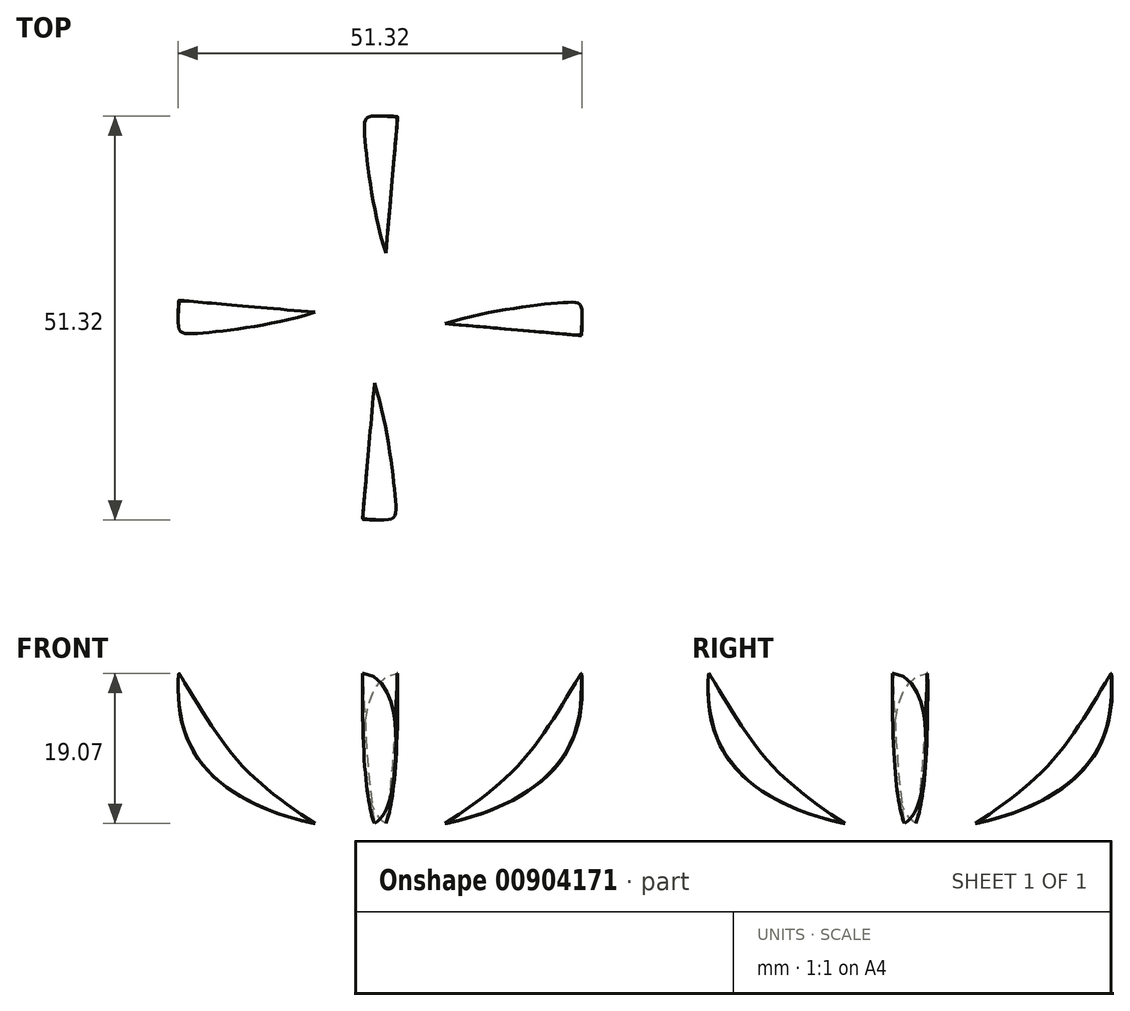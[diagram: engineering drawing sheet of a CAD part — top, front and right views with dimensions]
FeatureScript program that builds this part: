
annotation { "Feature Type Name" : "Feature", "Feature Type Description" : "" }
export const myFeature = defineFeature(function(context is Context, id is Id, definition is map)
    precondition{}
    {
        {
            var Q0;
            Q0=qCreatedBy(makeId("Front.planeOp"),FACE);
            var sketch = newSketch(context, id + "F0", { "sketchPlane" : qUnion([Q0])});
            skLineSegment(sketch, "E0", {"start": v(-28.58, 0) * mm, "end": v(28.58, 0) * mm, "construction": true});
            skLineSegment(sketch, "E1", {"start": v(0, 0) * mm, "end": v(0, -50.8) * mm, "construction": true});
            skLineSegment(sketch, "E2", {"start": v(-12.7, -50.8) * mm, "end": v(12.7, -50.8) * mm, "construction": true});
            skLineSegment(sketch, "E3", {"start": v(0, 0) * mm, "end": v(0, -12.7) * mm, "construction": true});
            skLineSegment(sketch, "E4", {"start": v(-23.5, -12.7) * mm, "end": v(23.5, -12.7) * mm, "construction": true});
            skLineSegment(sketch, "E5", {"start": v(0, -50.8) * mm, "end": v(0, -38.1) * mm, "construction": true});
            skLineSegment(sketch, "E6", {"start": v(-25.4, -38.1) * mm, "end": v(25.4, -38.1) * mm, "construction": true});
            skLineSegment(sketch, "E7", {"start": v(0, -52.8) * mm, "end": v(0, -57.57) * mm, "construction": true});
            skLineSegment(sketch, "E8", {"start": v(-19.77, -52.8) * mm, "end": v(-17.38, -48.69) * mm, "construction": true});
            skLineSegment(sketch, "E9", {"start": v(-28.25, -13.02) * mm, "end": v(-23.5, -12.7) * mm, "construction": true});
            skLineSegment(sketch, "E10", {"start": v(23.5, -12.7) * mm, "end": v(28.25, -12.93) * mm, "construction": true});
            skLineSegment(sketch, "E11", {"start": v(-25.4, -38.1) * mm, "end": v(-29.76, -40.01) * mm, "construction": true});
            skLineSegment(sketch, "E12", {"start": v(25.4, -38.1) * mm, "end": v(30.07, -39.03) * mm, "construction": true});
            skLineSegment(sketch, "E13", {"start": v(16.77, -49.02) * mm, "end": v(19.05, -53.2) * mm, "construction": true});
            skLineSegment(sketch, "E14", {"start": v(-28.58, 0) * mm, "end": v(-34.9, -3.29) * mm, "construction": true});
            skLineSegment(sketch, "E15", {"start": v(28.58, 0) * mm, "end": v(34.58, -3.85) * mm, "construction": true});
            skLineSegment(sketch, "E16", {"start": v(0, -52.8) * mm, "end": v(0, -57.57) * mm});
            skFitSpline(sketch, "E17", {"points": [v(0, -57.57) * mm, v(19.05, -53.2) * mm, v(30.07, -39.03) * mm, v(28.25, -12.93) * mm, v(34.58, -3.85) * mm, v(28.57, 0) * mm, v(23.5, -12.7) * mm, v(25.4, -38.1) * mm, v(16.77, -49.02) * mm, v(0, -52.8) * mm, v(-17.38, -48.69) * mm, v(-25.4, -38.1) * mm, v(-23.5, -12.7) * mm, v(-28.57, 0) * mm, v(-34.9, -3.29) * mm, v(-28.25, -13.02) * mm, v(-29.76, -40.01) * mm, v(-19.77, -52.8) * mm, v(0, -57.57) * mm]});
            skLineSegment(sketch, "E18", {"start": v(-25.62, -32.87) * mm, "end": v(-29.42, -32.87) * mm, "construction": true});
            skFitSpline(sketch, "E19", {"points": [v(-25.62, -32.87) * mm, v(-4.79, -52.5) * mm], "startDerivative": vector(17.85, -29.52) * mm, "endDerivative": vector(38.14, -17.66) * mm});
            skSolve(sketch);
        }
        {
            var Q0;
            {var subQ0=sQuery(id+"F0.wireOp",EDGE,"j9txepCX-qMbL-OIfj-HFUU-9PL2DQeBk5dc");var subQ1=sQuery(id+"F0.wireOp",EDGE,"E17");var subQ3=makeQuery(id+"F0.imprint","INTERSECT",VERTEX,{"derivedFrom":[subQ1,subQ0]});Q0=makeQuery(id+"F0.imprint","IMPRINT",FACE,{"disambiguationData":[TD([[makeQuery(id+"F0.imprint","IMPRINT",EDGE,{"disambiguationData":[TD([[subQ3,-1.0]])],"derivedFrom":subQ1}),-1.0]])]});}
            var Q1;
            Q1=sQuery(id+"F0.wireOp",EDGE,"E1");
            revolve(context, id + "F1", {"surfaceOperationType" : NewSurfaceOperationType.NEW, "entities" : qUnion([Q0]), "axis" : qUnion([Q1]), "revolveType" : RevolveType.TWO_DIRECTIONS, "angle" : 5 * degree, "angleBack" : 355 * degree});
        }
        {
            var Q0;
            {var subQ0=sQuery(id+"F0.wireOp",EDGE,"j9txepCX-qMbL-OIfj-HFUU-9PL2DQeBk5dc");var subQ1=sQuery(id+"F0.wireOp",EDGE,"E17");var subQ3=makeQuery(id+"F0.imprint","INTERSECT",VERTEX,{"derivedFrom":[subQ1,subQ0]});Q0=makeQuery(id+"F0.imprint","IMPRINT",FACE,{"disambiguationData":[TD([[makeQuery(id+"F0.imprint","IMPRINT",EDGE,{"disambiguationData":[TD([[subQ3,-1.0]])],"derivedFrom":subQ1}),-1.0]])]});}
            var Q1;
            Q1=sQuery(id+"F0.wireOp",EDGE,"E5");
            revolve(context, id + "F2", {"surfaceOperationType" : NewSurfaceOperationType.NEW, "entities" : qUnion([Q0]), "axis" : qUnion([Q1]), "revolveType" : RevolveType.TWO_DIRECTIONS, "angle" : 185 * degree, "angleBack" : 175 * degree});
        }
        {
            var Q0;
            {var subQ0=sQuery(id+"F0.wireOp",EDGE,"j9txepCX-qMbL-OIfj-HFUU-9PL2DQeBk5dc");var subQ1=sQuery(id+"F0.wireOp",EDGE,"E17");var subQ3=makeQuery(id+"F0.imprint","INTERSECT",VERTEX,{"derivedFrom":[subQ1,subQ0]});Q0=makeQuery(id+"F0.imprint","IMPRINT",FACE,{"disambiguationData":[TD([[makeQuery(id+"F0.imprint","IMPRINT",EDGE,{"disambiguationData":[TD([[subQ3,-1.0]])],"derivedFrom":subQ1}),-1.0]])]});}
            var Q1;
            Q1=sQuery(id+"F0.wireOp",EDGE,"E5");
            revolve(context, id + "F3", {"surfaceOperationType" : NewSurfaceOperationType.NEW, "entities" : qUnion([Q0]), "axis" : qUnion([Q1]), "revolveType" : RevolveType.TWO_DIRECTIONS, "angle" : 275 * degree, "angleBack" : 265 * degree});
        }
        {
            var Q0;
            {var subQ0=sQuery(id+"F0.wireOp",EDGE,"j9txepCX-qMbL-OIfj-HFUU-9PL2DQeBk5dc");var subQ1=sQuery(id+"F0.wireOp",EDGE,"E17");var subQ3=makeQuery(id+"F0.imprint","INTERSECT",VERTEX,{"derivedFrom":[subQ1,subQ0]});Q0=makeQuery(id+"F0.imprint","IMPRINT",FACE,{"disambiguationData":[TD([[makeQuery(id+"F0.imprint","IMPRINT",EDGE,{"disambiguationData":[TD([[subQ3,-1.0]])],"derivedFrom":subQ1}),-1.0]])]});}
            var Q1;
            Q1=sQuery(id+"F0.wireOp",EDGE,"E5");
            revolve(context, id + "F4", {"surfaceOperationType" : NewSurfaceOperationType.NEW, "entities" : qUnion([Q0]), "axis" : qUnion([Q1]), "revolveType" : RevolveType.TWO_DIRECTIONS, "angle" : 95 * degree, "angleBack" : 85 * degree});
        }
        {
            var Q0;
            Q0=makeQuery(id+"F4.opRevolve","CAP_EDGE",EDGE,{"disambiguationData":[OSD([sQuery(id+"F0.wireOp",EDGE,"E19")])],"isStart":false});
            var Q1;
            Q1=makeQuery(id+"F1.opRevolve","CAP_EDGE",EDGE,{"disambiguationData":[OSD([sQuery(id+"F0.wireOp",EDGE,"E19")])],"isStart":true});
            var Q2;
            Q2=makeQuery(id+"F3.opRevolve","CAP_EDGE",EDGE,{"disambiguationData":[OSD([sQuery(id+"F0.wireOp",EDGE,"E19")])],"isStart":false});
            var Q3;
            Q3=makeQuery(id+"F2.opRevolve","CAP_EDGE",EDGE,{"disambiguationData":[OSD([sQuery(id+"F0.wireOp",EDGE,"E19")])],"isStart":false});
            fillet(context, id + "F5", {"entities" : qUnion([Q0, Q1, Q2, Q3]), "tangentPropagation" : true, "radius" : 5.08 * mm, "defaultsChanged" : false, "vertexSettings" : [], "allowEdgeOverflow" : false});
        }
    });
